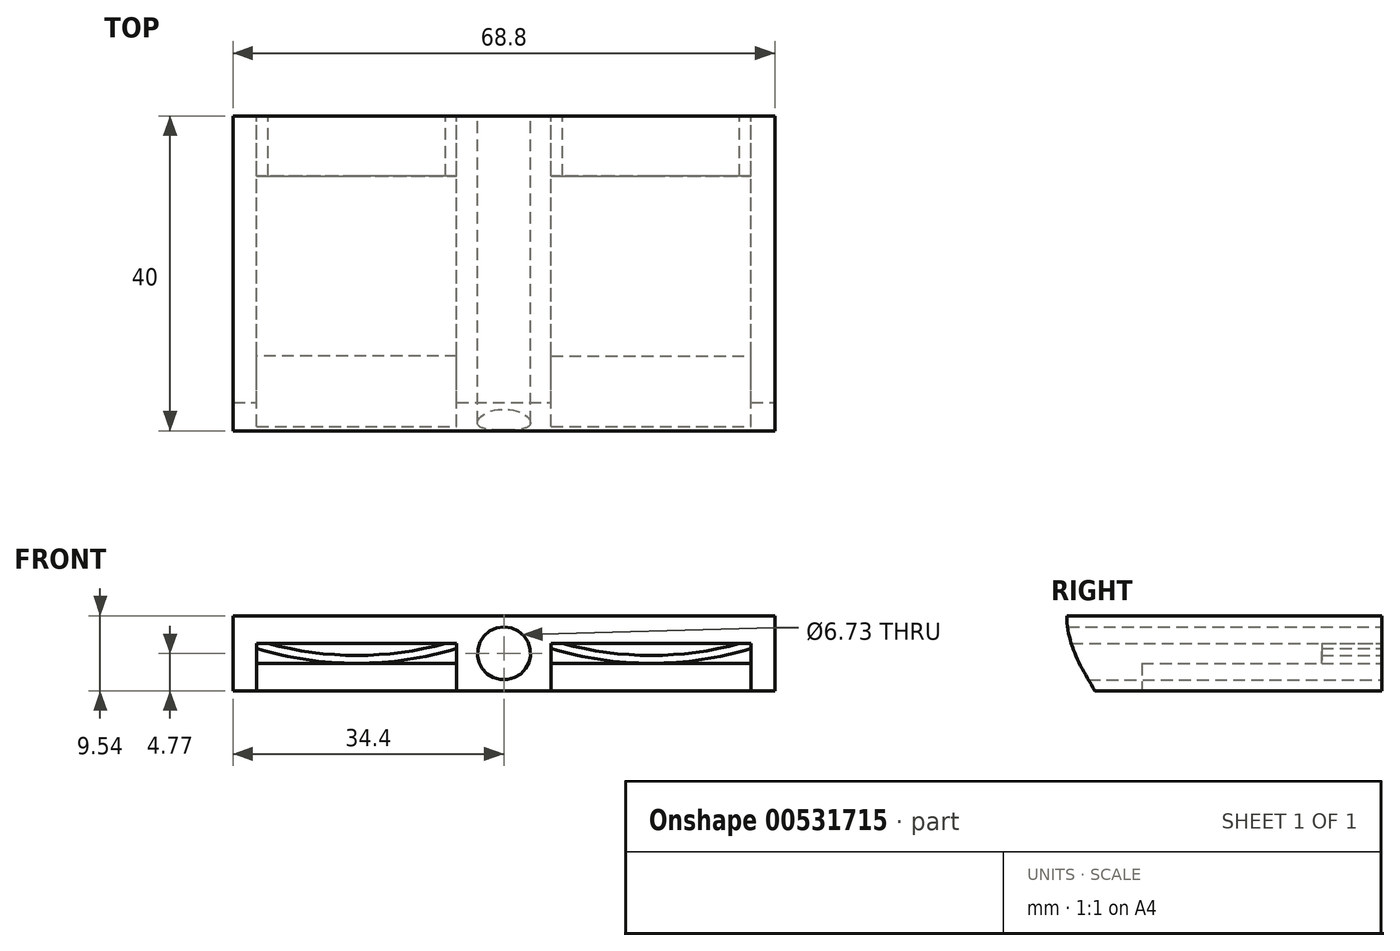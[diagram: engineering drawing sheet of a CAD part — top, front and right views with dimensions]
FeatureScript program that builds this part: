
annotation { "Feature Type Name" : "Feature", "Feature Type Description" : "" }
export const myFeature = defineFeature(function(context is Context, id is Id, definition is map)
    precondition{}
    {
        {
            var Q0;
            Q0=qCreatedBy(makeId("Front.planeOp"),FACE);
            var sketch = newSketch(context, id + "F0", { "sketchPlane" : qUnion([Q0])});
            skLineSegment(sketch, "E0.bottom", {"start": v(0, 0) * mm, "end": v(25.4, 0) * mm});
            skLineSegment(sketch, "E0.top", {"start": v(0, 2.54) * mm, "end": v(25.4, 2.54) * mm});
            skLineSegment(sketch, "E0.left", {"start": v(0, 0) * mm, "end": v(0, 2.54) * mm});
            skLineSegment(sketch, "E0.right", {"start": v(25.4, 0) * mm, "end": v(25.4, 2.54) * mm});
            skLineSegment(sketch, "E1.bottom", {"start": v(37.4, 0) * mm, "end": v(62.8, 0) * mm});
            skLineSegment(sketch, "E1.top", {"start": v(37.4, 2.54) * mm, "end": v(62.8, 2.54) * mm});
            skLineSegment(sketch, "E1.left", {"start": v(37.4, 0) * mm, "end": v(37.4, 2.54) * mm});
            skLineSegment(sketch, "E1.right", {"start": v(62.8, 0) * mm, "end": v(62.8, 2.54) * mm});
            skLineSegment(sketch, "E2.bottom", {"start": v(-3, 6.04) * mm, "end": v(65.8, 6.04) * mm});
            skLineSegment(sketch, "E2.top", {"start": v(-3, -3.5) * mm, "end": v(65.8, -3.5) * mm});
            skLineSegment(sketch, "E2.left", {"start": v(-3, 6.04) * mm, "end": v(-3, -3.5) * mm});
            skLineSegment(sketch, "E2.right", {"start": v(65.8, 6.04) * mm, "end": v(65.8, -3.5) * mm});
            skLineSegment(sketch, "E3", {"start": v(25.4, 1.27) * mm, "end": v(37.4, 1.27) * mm, "construction": true});
            skPoint(sketch, "E4.middle", {"position": v(31.4, 1.27) * mm});
            skCircle(sketch, "E5", {"center": v(31.4, 1.27) * mm, "radius": 3.37 * mm});
            skSolve(sketch);
        }
        {
            var Q0;
            Q0 = qSketchRegion(id + "F0", true);
            extrude(context, id + "F1", {"entities" : qUnion([Q0]), "depth" : 40 * mm, "offsetDistance" : 25.4 * mm});
        }
        {
            var Q0;
            Q0=makeQuery(id+"F1.opExtrude","SWEPT_FACE",FACE,{"disambiguationData":[OSD([sQuery(id+"F0.wireOp",EDGE,"E2.top")])]});
            var sketch = newSketch(context, id + "F2", { "sketchPlane" : qUnion([Q0])});
            skLineSegment(sketch, "E6.bottom", {"start": v(25.4, 40) * mm, "end": v(0, 40) * mm});
            skLineSegment(sketch, "E6.top", {"start": v(25.4, 30.48) * mm, "end": v(0, 30.48) * mm});
            skLineSegment(sketch, "E6.left", {"start": v(25.4, 40) * mm, "end": v(25.4, 30.48) * mm});
            skLineSegment(sketch, "E6.right", {"start": v(0, 40) * mm, "end": v(0, 30.48) * mm});
            skLineSegment(sketch, "E7.bottom", {"start": v(37.4, 40) * mm, "end": v(62.8, 40) * mm});
            skLineSegment(sketch, "E7.top", {"start": v(37.4, 30.48) * mm, "end": v(62.8, 30.48) * mm});
            skLineSegment(sketch, "E7.left", {"start": v(37.4, 40) * mm, "end": v(37.4, 30.48) * mm});
            skLineSegment(sketch, "E7.right", {"start": v(62.8, 40) * mm, "end": v(62.8, 30.48) * mm});
            skSolve(sketch);
        }
        {
            var Q0;
            Q0 = qSketchRegion(id + "F2", true);
            extrude(context, id + "F3", {"entities" : qUnion([Q0]), "operationType" : NewBodyOperationType.REMOVE, "endBound" : BoundingType.UP_TO_NEXT, "oppositeDirection" : true, "depth" : 25.4 * mm, "offsetDistance" : 25.4 * mm});
        }
        {
            var Q0;
            Q0=makeQuery(id+"F1.opExtrude","CAP_FACE",FACE,{"disambiguationData":[OSD([sQuery(id+"F0.wireOp",EDGE,"E0.bottom"),sQuery(id+"F0.wireOp",EDGE,"E0.top"),sQuery(id+"F0.wireOp",EDGE,"E0.left"),sQuery(id+"F0.wireOp",EDGE,"E0.right"),sQuery(id+"F0.wireOp",EDGE,"E1.bottom"),sQuery(id+"F0.wireOp",EDGE,"E1.top"),sQuery(id+"F0.wireOp",EDGE,"E1.left"),sQuery(id+"F0.wireOp",EDGE,"E1.right"),sQuery(id+"F0.wireOp",EDGE,"E2.bottom"),sQuery(id+"F0.wireOp",EDGE,"E2.top"),sQuery(id+"F0.wireOp",EDGE,"E2.left"),sQuery(id+"F0.wireOp",EDGE,"E2.right"),sQuery(id+"F0.wireOp",EDGE,"E5")])],"isStart":true});
            var sketch = newSketch(context, id + "F4", { "sketchPlane" : qUnion([Q0])});
            skCircle(sketch, "E8", {"center": v(-31.4, 1.27) * mm, "radius": 3.9 * mm});
            skSolve(sketch);
        }
        {
            var Q0;
            Q0=makeQuery(id+"F1.opExtrude","SWEPT_FACE",FACE,{"disambiguationData":[OSD([sQuery(id+"F0.wireOp",EDGE,"E2.right")])]});
            var sketch = newSketch(context, id + "F5", { "sketchPlane" : qUnion([Q0])});
            skLineSegment(sketch, "E9", {"start": v(-36.41, -3.5) * mm, "end": v(-40, -3.5) * mm});
            skLineSegment(sketch, "E10", {"start": v(-40, -3.5) * mm, "end": v(-40, 6.04) * mm});
            skFitSpline(sketch, "E11", {"points": [v(-40, 6.04) * mm, v(-36.41, -3.5) * mm], "startDerivative": vector(0, -10.53) * mm, "endDerivative": vector(5.67, -9.32) * mm});
            skSolve(sketch);
        }
        {
            var Q0;
            Q0 = qSketchRegion(id + "F5", true);
            var Q1;
            Q1=makeQuery(id+"F1.opExtrude","SWEPT_FACE",FACE,{"disambiguationData":[OSD([sQuery(id+"F0.wireOp",EDGE,"E2.left")])]});
            extrude(context, id + "F6", {"entities" : qUnion([Q0]), "operationType" : NewBodyOperationType.REMOVE, "endBound" : BoundingType.UP_TO_SURFACE, "oppositeDirection" : true, "depth" : 25.4 * mm, "endBoundEntityFace" : qUnion([Q1]), "offsetDistance" : 25.4 * mm});
        }
        {
            var Q0;
            Q0=makeQuery(id+"F4.imprint","IMPRINT",FACE,{"disambiguationData":[TD([[makeQuery(id+"F4.imprint","IMPRINT",EDGE,{"derivedFrom":sQuery(id+"F4.wireOp",EDGE,"E8")}),-1.0]])]});
            var sketch = newSketch(context, id + "F7", { "sketchPlane" : qUnion([Q0])});
            skArc(sketch, "E12", {"start": v(-62.8, 1.9) * mm, "mid": v(-50.1, 0) * mm, "end": v(-37.4, 1.9) * mm});
            skPoint(sketch, "E13", {"position": v(-50.1, 0) * mm});
            skLineSegment(sketch, "E14", {"start": v(-62.8, 2.54) * mm, "end": v(-62.8, 1.27) * mm, "construction": true});
            skPoint(sketch, "E15", {"position": v(-62.8, 1.9) * mm});
            skArc(sketch, "E16.0", {"start": v(-61.35, 2.54) * mm, "mid": v(-50.1, 1.02) * mm, "end": v(-38.85, 2.54) * mm});
            skLineSegment(sketch, "E17", {"start": v(-61.35, 2.54) * mm, "end": v(-38.85, 2.54) * mm});
            skLineSegment(sketch, "E18", {"start": v(-62.8, 1.9) * mm, "end": v(-62.8, 0) * mm});
            skLineSegment(sketch, "E19", {"start": v(-62.8, 0) * mm, "end": v(-37.4, 0) * mm});
            skLineSegment(sketch, "E20", {"start": v(-37.4, 0) * mm, "end": v(-37.4, 1.9) * mm});
            skLineSegment(sketch, "E21", {"start": v(-31.4, 6.04) * mm, "end": v(-31.4, -8.18) * mm, "construction": true});
            skLineSegment(sketch, "E22.MirrorCS", {"start": v(-25.4, 0) * mm, "end": v(-25.4, 1.9) * mm});
            skArc(sketch, "E23.MirrorCS", {"start": v(0, 1.9) * mm, "mid": v(-12.7, 0) * mm, "end": v(-25.4, 1.9) * mm});
            skLineSegment(sketch, "E24.MirrorCS", {"start": v(0, 0) * mm, "end": v(-25.4, 0) * mm});
            skLineSegment(sketch, "E25.MirrorCS", {"start": v(0, 1.9) * mm, "end": v(0, 0) * mm});
            skLineSegment(sketch, "E26.MirrorCS", {"start": v(-1.45, 2.54) * mm, "end": v(-23.95, 2.54) * mm});
            skArc(sketch, "E27.MirrorCS", {"start": v(-1.45, 2.54) * mm, "mid": v(-12.7, 1.02) * mm, "end": v(-23.95, 2.54) * mm});
            skSolve(sketch);
        }
        {
            var Q0;
            Q0 = qSketchRegion(id + "F7", true);
            extrude(context, id + "F8", {"entities" : qUnion([Q0]), "operationType" : NewBodyOperationType.ADD, "oppositeDirection" : true, "depth" : 7.62 * mm, "offsetDistance" : 25.4 * mm});
        }
    });
